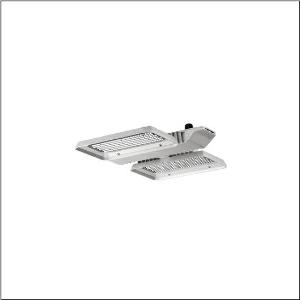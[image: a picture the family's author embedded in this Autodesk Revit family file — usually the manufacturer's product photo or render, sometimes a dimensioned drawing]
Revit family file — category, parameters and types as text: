
# Revit family: highbay_11_51hl61d14dca
name_source: partatom
category: Lighting Fixtures
units: mm (PartAtom-declared; Revit-internal decimal feet)

## family parameters
Cut with Voids When Loaded = No
Host = Face
Light Source = No
Part Type = Normal
Room Calculation Point = No
Round Connector Dimension = Use Diameter
Shared = No

## types (1)
- --- (1 x LED, 9790 lm, 55.6 W, 4000K)
    Apparent Load = 56 VA
    CIE Flux Codes = 88 95 99 100 99
    Color Rendering = 80
    Color Temperature = 4000K
    Default Elevation = 1800 mm
    Description = Highbay 11, LED high bay luminaire, primary light control with lens, of PMMA, light emission: direct distribution, primary light characteristic: symmetric, installation type: surface-mounted, suspended mounting, for 1x 2x LED, rated luminous flux: 9.790lm, luminous efficacy: 176lm/W, light colour: 840, colour temperature: 4000K, control gear: ECG DALI, with terminal, 5-pole, max. 2.5mm², mains connection: 230..240V, AC, 50/60Hz, rated input power: 56W, LED unit, of diecast aluminium, coated, metallic grey (RAL 9006), length: 470mm, width: 500mm, height: 65mm, housing, of diecast aluminium, coated, metallic grey (RAL 9006), protection rating (complete): IP65, insulation class (complete): insulation class I (protective earthing), certification: CE, ENEC, VDE, UKCA, protection symbol: D, impact resistance: IK08 with glass or PC cover, permissible operating ambient temperature: -35..+70°C, corresponds to IFS (International Featured Standards) requirements for safety and quality in the food industry, reducing of maximum allowable ambient temperature of 5°C with ceiling mounting, packaging unit: 1 piece
    Height = 95 mm
    Lamp = 1 x LED
    Lamp Light Flux = 9790 lm
    Lamp Power = 55.6 W
    Lamp count = 1
    Length = 468 mm
    Luminous efficacy = 176 lm/W
    Manufacturer = Siteco
    ModVariant = No
    Model = 51HL61D14DCA
    Mounting Place = Ceiling
    Mounting Type = Pendant
    Number of Poles = 1
    OnlyDefault = Yes
    Power Factor = 1
    Product Name = Highbay 11
    Product group = LED high bay luminaire
    ProductGroupID = 903
    Protection Class = Protection class I
    Protection Degree = IP 65
    RLX_Detail_Level = 1
    RLX_Emergency_Light_Flux = 0 lm
    RLX_Emergency_Type = 0
    RLX_Emergency_Type_DB = No
    RlxData = <blob elided: 70625 chars, md5=184518bd>
    Socket = socket
    Standby Power = 0 W
    System Light Flux = 9790 lm
    System Power = 56 W
    Type Comments = factory setting: luminous flux: 100 % | dim-lin: 254 | 315 mA
    Type Image = l_1003425.jpg
    URL = http://relux.com
    VarID = @adj_146079
    Voltage = 0 V
    Weight = 0.00 kg
    Width = 501 mm

## geometry (parser evidence)
native form markers: Blend x4, Sweep x11
no freeform markers — native parametric forms only
